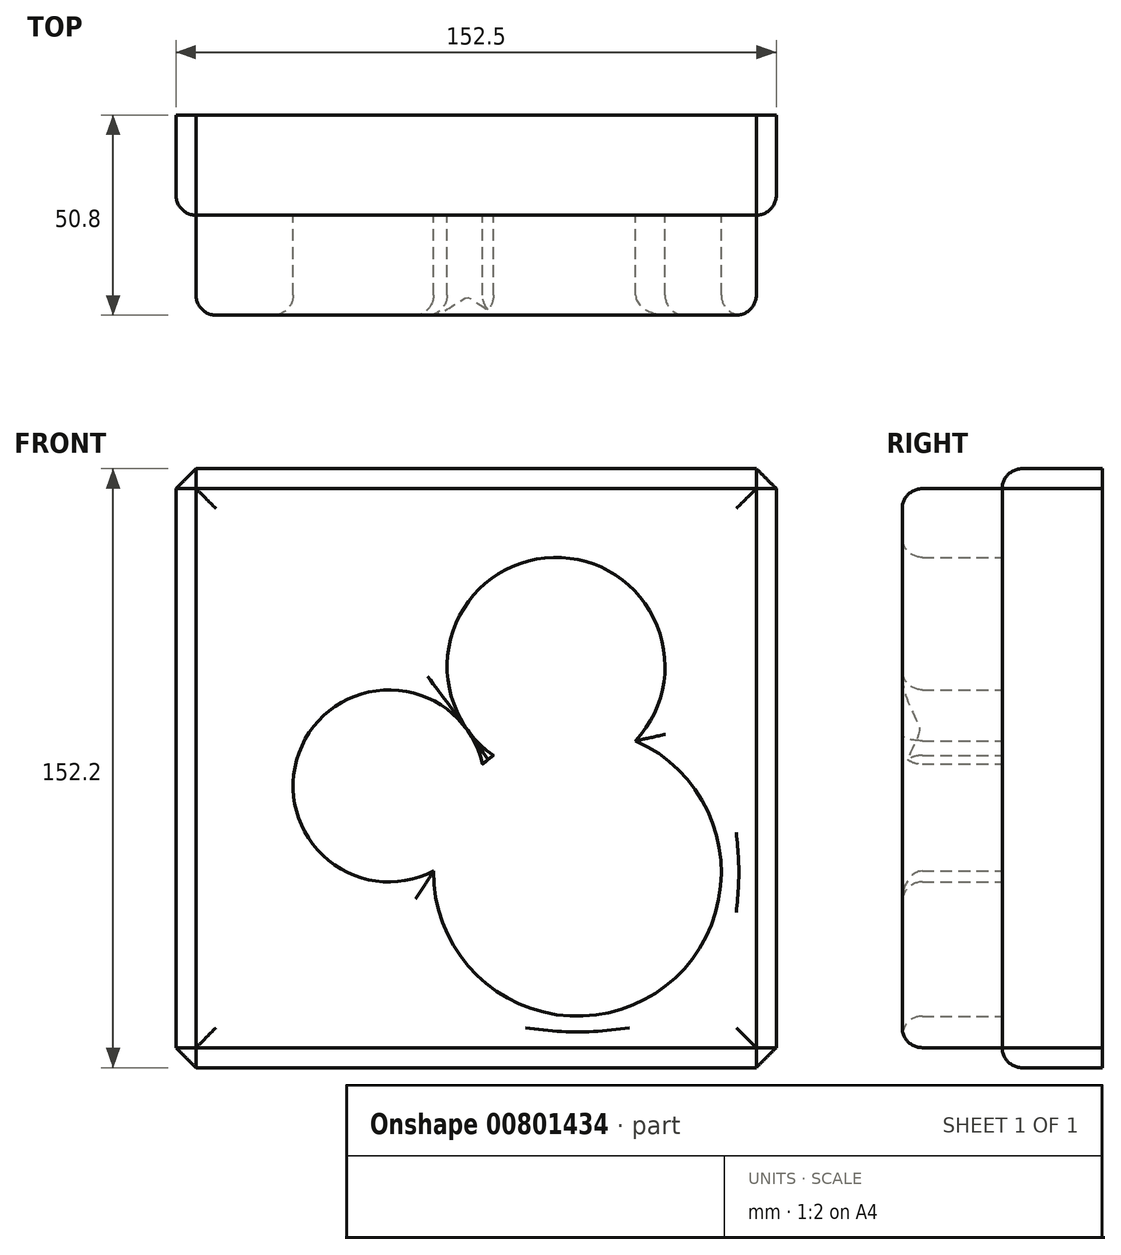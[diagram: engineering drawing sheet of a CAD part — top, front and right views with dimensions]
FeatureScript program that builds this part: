
annotation { "Feature Type Name" : "Feature", "Feature Type Description" : "" }
export const myFeature = defineFeature(function(context is Context, id is Id, definition is map)
    precondition{}
    {
        {
            var Q0;
            Q0=qCreatedBy(makeId("Front.planeOp"),FACE);
            var sketch = newSketch(context, id + "F0", { "sketchPlane" : qUnion([Q0])});
            skLineSegment(sketch, "E0.bottom", {"start": v(0, 0) * mm, "end": v(76.25, 0) * mm});
            skLineSegment(sketch, "E0.top", {"start": v(0, 76.25) * mm, "end": v(76.25, 76.25) * mm});
            skLineSegment(sketch, "E0.left", {"start": v(0, 0) * mm, "end": v(0, 76.25) * mm});
            skLineSegment(sketch, "E0.right", {"start": v(76.25, 0) * mm, "end": v(76.25, 76.25) * mm});
            skLineSegment(sketch, "E1.bottom", {"start": v(0, 0) * mm, "end": v(-76.25, 0) * mm});
            skLineSegment(sketch, "E1.top", {"start": v(0, -75.95) * mm, "end": v(-76.25, -75.95) * mm});
            skLineSegment(sketch, "E1.left", {"start": v(0, 0) * mm, "end": v(0, -75.95) * mm});
            skLineSegment(sketch, "E1.right", {"start": v(-76.25, 0) * mm, "end": v(-76.25, -75.95) * mm});
            skLineSegment(sketch, "E2.bottom", {"start": v(76.25, -75.95) * mm, "end": v(0, -75.95) * mm});
            skLineSegment(sketch, "E2.top", {"start": v(76.25, 0) * mm, "end": v(0, 0) * mm});
            skLineSegment(sketch, "E2.left", {"start": v(76.25, -75.95) * mm, "end": v(76.25, 0) * mm});
            skLineSegment(sketch, "E2.right", {"start": v(0, -75.95) * mm, "end": v(0, 0) * mm});
            skLineSegment(sketch, "E3.top", {"start": v(0, 76.25) * mm, "end": v(-76.25, 76.25) * mm});
            skLineSegment(sketch, "E3.right", {"start": v(-76.25, 0) * mm, "end": v(-76.25, 76.25) * mm});
            skSolve(sketch);
        }
        {
            var Q0;
            Q0=makeQuery(id+"F0.imprint","IMPRINT",FACE,{"disambiguationData":[TD([[makeQuery(id+"F0.imprint","IMPRINT",EDGE,{"derivedFrom":sQuery(id+"F0.wireOp",EDGE,"E1.bottom")}),-1.0]])]});
            var Q1;
            Q1=makeQuery(id+"F0.imprint","IMPRINT",FACE,{"disambiguationData":[TD([[makeQuery(id+"F0.imprint","IMPRINT",EDGE,{"derivedFrom":sQuery(id+"F0.wireOp",EDGE,"E0.top")}),-1.0]])]});
            var Q2;
            Q2=makeQuery(id+"F0.imprint","IMPRINT",FACE,{"disambiguationData":[TD([[makeQuery(id+"F0.imprint","IMPRINT",EDGE,{"derivedFrom":sQuery(id+"F0.wireOp",EDGE,"E2.bottom")}),-1.0]])]});
            var Q3;
            Q3=makeQuery(id+"F0.imprint","IMPRINT",FACE,{"disambiguationData":[TD([[makeQuery(id+"F0.imprint","IMPRINT",EDGE,{"derivedFrom":sQuery(id+"F0.wireOp",EDGE,"E1.top")}),-1.0]])]});
            extrude(context, id + "F1", {"entities" : qUnion([Q0, Q1, Q2, Q3]), "depth" : 25.4 * mm, "offsetDistance" : 25.4 * mm});
        }
        {
            var Q0;
            Q0=makeQuery(id+"F1.opExtrude","CAP_EDGE",EDGE,{"disambiguationData":[OSD([sQuery(id+"F0.wireOp",EDGE,"E0.top"),sQuery(id+"F0.wireOp",EDGE,"E3.top")])],"isStart":false});
            var Q1;
            Q1=makeQuery(id+"F1.opExtrude","CAP_EDGE",EDGE,{"disambiguationData":[OSD([sQuery(id+"F0.wireOp",EDGE,"E1.right"),sQuery(id+"F0.wireOp",EDGE,"E3.right")])],"isStart":false});
            var Q2;
            Q2=makeQuery(id+"F1.opExtrude","CAP_EDGE",EDGE,{"disambiguationData":[OSD([sQuery(id+"F0.wireOp",EDGE,"E1.top"),sQuery(id+"F0.wireOp",EDGE,"E2.bottom")])],"isStart":false});
            var Q3;
            Q3=makeQuery(id+"F1.opExtrude","CAP_EDGE",EDGE,{"disambiguationData":[OSD([sQuery(id+"F0.wireOp",EDGE,"E0.right"),sQuery(id+"F0.wireOp",EDGE,"E2.left")])],"isStart":false});
            fillet(context, id + "F2", {"entities" : qUnion([Q0, Q1, Q2, Q3]), "radius" : 5.08 * mm, "tangentPropagation" : true, "allowEdgeOverflow" : false});
        }
        {
            var Q0;
            Q0=makeQuery(id+"F2.opFillet","BLEND_EDGE",EDGE,{"blendedFrom":[makeQuery(id+"F1.opExtrude","CAP_EDGE",EDGE,{"disambiguationData":[OSD([sQuery(id+"F0.wireOp",EDGE,"E0.top"),sQuery(id+"F0.wireOp",EDGE,"E3.top")])],"isStart":false}),makeQuery(id+"F1.opExtrude","CAP_EDGE",EDGE,{"disambiguationData":[OSD([sQuery(id+"F0.wireOp",EDGE,"E1.right"),sQuery(id+"F0.wireOp",EDGE,"E3.right")])],"isStart":false})],"blendedInto":[]});
            var Q1;
            Q1=makeQuery(id+"F2.opFillet","BLEND_EDGE",EDGE,{"blendedFrom":[makeQuery(id+"F1.opExtrude","CAP_EDGE",EDGE,{"disambiguationData":[OSD([sQuery(id+"F0.wireOp",EDGE,"E0.top"),sQuery(id+"F0.wireOp",EDGE,"E3.top")])],"isStart":false}),makeQuery(id+"F1.opExtrude","CAP_EDGE",EDGE,{"disambiguationData":[OSD([sQuery(id+"F0.wireOp",EDGE,"E0.right"),sQuery(id+"F0.wireOp",EDGE,"E2.left")])],"isStart":false})],"blendedInto":[]});
            var Q2;
            Q2=makeQuery(id+"F2.opFillet","BLEND_EDGE",EDGE,{"blendedFrom":[makeQuery(id+"F1.opExtrude","CAP_EDGE",EDGE,{"disambiguationData":[OSD([sQuery(id+"F0.wireOp",EDGE,"E0.right"),sQuery(id+"F0.wireOp",EDGE,"E2.left")])],"isStart":false}),makeQuery(id+"F1.opExtrude","CAP_EDGE",EDGE,{"disambiguationData":[OSD([sQuery(id+"F0.wireOp",EDGE,"E1.top"),sQuery(id+"F0.wireOp",EDGE,"E2.bottom")])],"isStart":false})],"blendedInto":[]});
            var Q3;
            Q3=makeQuery(id+"F2.opFillet","BLEND_EDGE",EDGE,{"blendedFrom":[makeQuery(id+"F1.opExtrude","CAP_EDGE",EDGE,{"disambiguationData":[OSD([sQuery(id+"F0.wireOp",EDGE,"E1.top"),sQuery(id+"F0.wireOp",EDGE,"E2.bottom")])],"isStart":false}),makeQuery(id+"F1.opExtrude","CAP_EDGE",EDGE,{"disambiguationData":[OSD([sQuery(id+"F0.wireOp",EDGE,"E1.right"),sQuery(id+"F0.wireOp",EDGE,"E3.right")])],"isStart":false})],"blendedInto":[]});
            chamfer(context, id + "F3", {"entities" : qUnion([Q0, Q1, Q2, Q3]), "width" : 5.08 * mm, "tangentPropagation" : true});
        }
        {
            var Q0;
            Q0=makeQuery(id+"F1.opExtrude","CAP_FACE",FACE,{"disambiguationData":[OSD([sQuery(id+"F0.wireOp",EDGE,"E0.top"),sQuery(id+"F0.wireOp",EDGE,"E0.right"),sQuery(id+"F0.wireOp",EDGE,"E1.top"),sQuery(id+"F0.wireOp",EDGE,"E1.right"),sQuery(id+"F0.wireOp",EDGE,"E2.bottom"),sQuery(id+"F0.wireOp",EDGE,"E2.left"),sQuery(id+"F0.wireOp",EDGE,"E3.top"),sQuery(id+"F0.wireOp",EDGE,"E3.right")])],"isStart":false});
            var sketch = newSketch(context, id + "F4", { "sketchPlane" : qUnion([Q0])});
            skCircle(sketch, "E4", {"center": v(-22.1, -4.36) * mm, "radius": 24.4 * mm});
            skCircle(sketch, "E5", {"center": v(20.3, 26.02) * mm, "radius": 27.68 * mm});
            skCircle(sketch, "E6", {"center": v(25.72, -26.32) * mm, "radius": 36.55 * mm});
            skSolve(sketch);
        }
        {
            var Q0;
            {var subQ0=sQuery(id+"F4.wireOp",EDGE,"E6");var subQ1=sQuery(id+"F4.wireOp",EDGE,"E4");var subQ6=makeQuery(id+"F4.imprint","INTERSECT",VERTEX,{"disambiguationData":[OD(0.0)],"derivedFrom":[subQ1,subQ0]});Q0=makeQuery(id+"F4.imprint","IMPRINT",FACE,{"disambiguationData":[TD([[makeQuery(id+"F4.imprint","IMPRINT",EDGE,{"disambiguationData":[TD([[subQ6,-1.0]])],"derivedFrom":subQ1}),-1.0]])]});}
            extrude(context, id + "F5", {"entities" : qUnion([Q0]), "operationType" : NewBodyOperationType.ADD, "depth" : 25.4 * mm, "offsetDistance" : 25.4 * mm});
        }
        {
            var Q0;
            {var subQ0=sQuery(id+"F0.wireOp",EDGE,"E3.right");var subQ1=sQuery(id+"F0.wireOp",EDGE,"E3.top");var subQ2=sQuery(id+"F0.wireOp",EDGE,"E2.left");var subQ3=sQuery(id+"F0.wireOp",EDGE,"E2.bottom");var subQ4=sQuery(id+"F0.wireOp",EDGE,"E1.right");var subQ5=sQuery(id+"F0.wireOp",EDGE,"E1.top");var subQ6=sQuery(id+"F0.wireOp",EDGE,"E0.right");var subQ7=sQuery(id+"F0.wireOp",EDGE,"E0.top");Q0=makeQuery(id+"F5.opExtrude","CAP_EDGE",EDGE,{"disambiguationData":[OSD([subQ7,subQ6,subQ5,subQ4,subQ3,subQ2,subQ1,subQ0]),TDD([makeQuery(id+"F4.imprint","IMPRINT",EDGE,{"derivedFrom":makeQuery(id+"F2.opFillet","BLEND_EDGE",EDGE,{"blendedFrom":[makeQuery(id+"F1.opExtrude","CAP_EDGE",EDGE,{"disambiguationData":[OSD([subQ4,subQ0])],"isStart":false}),makeQuery(id+"F1.opExtrude","CAP_FACE",FACE,{"disambiguationData":[OSD([subQ7,subQ6,subQ5,subQ4,subQ3,subQ2,subQ1,subQ0])],"isStart":false})],"blendedInto":[makeQuery(id+"F1.opExtrude","CAP_FACE",FACE,{"disambiguationData":[OSD([subQ7,subQ6,subQ5,subQ4,subQ3,subQ2,subQ1,subQ0])],"isStart":false})]})})])],"isStart":false});}
            var Q1;
            {var subQ0=sQuery(id+"F0.wireOp",EDGE,"E3.right");var subQ1=sQuery(id+"F0.wireOp",EDGE,"E3.top");var subQ2=sQuery(id+"F0.wireOp",EDGE,"E2.left");var subQ3=sQuery(id+"F0.wireOp",EDGE,"E2.bottom");var subQ4=sQuery(id+"F0.wireOp",EDGE,"E1.right");var subQ5=sQuery(id+"F0.wireOp",EDGE,"E1.top");var subQ6=sQuery(id+"F0.wireOp",EDGE,"E0.right");var subQ7=sQuery(id+"F0.wireOp",EDGE,"E0.top");Q1=makeQuery(id+"F5.opExtrude","CAP_EDGE",EDGE,{"disambiguationData":[OSD([subQ7,subQ6,subQ5,subQ4,subQ3,subQ2,subQ1,subQ0]),TDD([makeQuery(id+"F4.imprint","IMPRINT",EDGE,{"derivedFrom":makeQuery(id+"F2.opFillet","BLEND_EDGE",EDGE,{"blendedFrom":[makeQuery(id+"F1.opExtrude","CAP_EDGE",EDGE,{"disambiguationData":[OSD([subQ6,subQ2])],"isStart":false}),makeQuery(id+"F1.opExtrude","CAP_FACE",FACE,{"disambiguationData":[OSD([subQ7,subQ6,subQ5,subQ4,subQ3,subQ2,subQ1,subQ0])],"isStart":false})],"blendedInto":[makeQuery(id+"F1.opExtrude","CAP_FACE",FACE,{"disambiguationData":[OSD([subQ7,subQ6,subQ5,subQ4,subQ3,subQ2,subQ1,subQ0])],"isStart":false})]})})])],"isStart":false});}
            var Q2;
            {var subQ0=sQuery(id+"F0.wireOp",EDGE,"E3.right");var subQ1=sQuery(id+"F0.wireOp",EDGE,"E3.top");var subQ2=sQuery(id+"F0.wireOp",EDGE,"E2.left");var subQ3=sQuery(id+"F0.wireOp",EDGE,"E2.bottom");var subQ4=sQuery(id+"F0.wireOp",EDGE,"E1.right");var subQ5=sQuery(id+"F0.wireOp",EDGE,"E1.top");var subQ6=sQuery(id+"F0.wireOp",EDGE,"E0.right");var subQ7=sQuery(id+"F0.wireOp",EDGE,"E0.top");Q2=makeQuery(id+"F5.opExtrude","CAP_EDGE",EDGE,{"disambiguationData":[OSD([subQ7,subQ6,subQ5,subQ4,subQ3,subQ2,subQ1,subQ0]),TDD([makeQuery(id+"F4.imprint","IMPRINT",EDGE,{"derivedFrom":makeQuery(id+"F2.opFillet","BLEND_EDGE",EDGE,{"blendedFrom":[makeQuery(id+"F1.opExtrude","CAP_EDGE",EDGE,{"disambiguationData":[OSD([subQ7,subQ1])],"isStart":false}),makeQuery(id+"F1.opExtrude","CAP_FACE",FACE,{"disambiguationData":[OSD([subQ7,subQ6,subQ5,subQ4,subQ3,subQ2,subQ1,subQ0])],"isStart":false})],"blendedInto":[makeQuery(id+"F1.opExtrude","CAP_FACE",FACE,{"disambiguationData":[OSD([subQ7,subQ6,subQ5,subQ4,subQ3,subQ2,subQ1,subQ0])],"isStart":false})]})})])],"isStart":false});}
            var Q3;
            {var subQ0=sQuery(id+"F0.wireOp",EDGE,"E3.right");var subQ1=sQuery(id+"F0.wireOp",EDGE,"E3.top");var subQ2=sQuery(id+"F0.wireOp",EDGE,"E2.left");var subQ3=sQuery(id+"F0.wireOp",EDGE,"E2.bottom");var subQ4=sQuery(id+"F0.wireOp",EDGE,"E1.right");var subQ5=sQuery(id+"F0.wireOp",EDGE,"E1.top");var subQ6=sQuery(id+"F0.wireOp",EDGE,"E0.right");var subQ7=sQuery(id+"F0.wireOp",EDGE,"E0.top");Q3=makeQuery(id+"F5.opExtrude","CAP_EDGE",EDGE,{"disambiguationData":[OSD([subQ7,subQ6,subQ5,subQ4,subQ3,subQ2,subQ1,subQ0]),TDD([makeQuery(id+"F4.imprint","IMPRINT",EDGE,{"derivedFrom":makeQuery(id+"F2.opFillet","BLEND_EDGE",EDGE,{"blendedFrom":[makeQuery(id+"F1.opExtrude","CAP_EDGE",EDGE,{"disambiguationData":[OSD([subQ5,subQ3])],"isStart":false}),makeQuery(id+"F1.opExtrude","CAP_FACE",FACE,{"disambiguationData":[OSD([subQ7,subQ6,subQ5,subQ4,subQ3,subQ2,subQ1,subQ0])],"isStart":false})],"blendedInto":[makeQuery(id+"F1.opExtrude","CAP_FACE",FACE,{"disambiguationData":[OSD([subQ7,subQ6,subQ5,subQ4,subQ3,subQ2,subQ1,subQ0])],"isStart":false})]})})])],"isStart":false});}
            var Q4;
            {var subQ0=sQuery(id+"F4.wireOp",EDGE,"E6");Q4=makeQuery(id+"F5.opExtrude","CAP_EDGE",EDGE,{"disambiguationData":[OSD([subQ0]),TDD([makeQuery(id+"F4.imprint","IMPRINT",EDGE,{"disambiguationData":[TD([[makeQuery(id+"F4.imprint","INTERSECT",VERTEX,{"disambiguationData":[OD(1.0)],"derivedFrom":[sQuery(id+"F4.wireOp",EDGE,"E4"),subQ0]}),-1.0]])],"derivedFrom":subQ0})])],"isStart":false});}
            var Q5;
            Q5=makeQuery(id+"F5.opExtrude","CAP_EDGE",EDGE,{"disambiguationData":[OSD([sQuery(id+"F4.wireOp",EDGE,"E4")])],"isStart":false});
            var Q6;
            Q6=makeQuery(id+"F5.opExtrude","CAP_EDGE",EDGE,{"disambiguationData":[OSD([sQuery(id+"F4.wireOp",EDGE,"E5")])],"isStart":false});
            fillet(context, id + "F6", {"entities" : qUnion([Q0, Q1, Q2, Q3, Q4, Q5, Q6]), "radius" : 5.08 * mm, "tangentPropagation" : true, "allowEdgeOverflow" : false});
        }
    });
